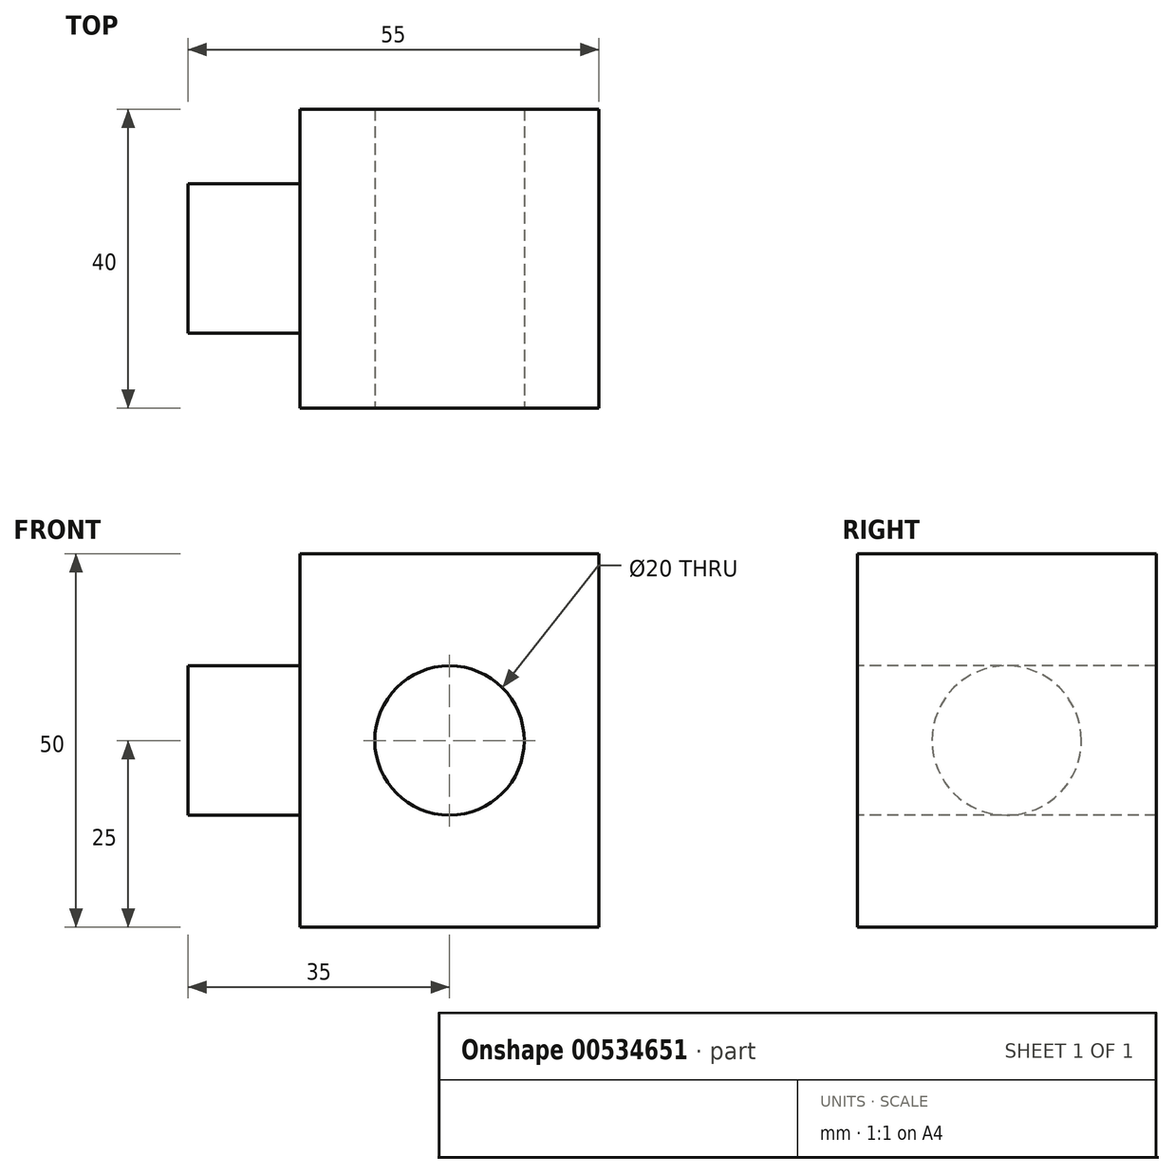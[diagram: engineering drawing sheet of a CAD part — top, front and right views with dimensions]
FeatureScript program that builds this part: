
annotation { "Feature Type Name" : "Feature", "Feature Type Description" : "" }
export const myFeature = defineFeature(function(context is Context, id is Id, definition is map)
    precondition{}
    {
        {
            var Q0;
            Q0=qCreatedBy(makeId("Right.planeOp"),FACE);
            var sketch = newSketch(context, id + "F0", { "sketchPlane" : qUnion([Q0])});
            skLineSegment(sketch, "E0.bottom", {"start": v(-20, 25) * mm, "end": v(20, 25) * mm});
            skLineSegment(sketch, "E0.top", {"start": v(-20, -25) * mm, "end": v(20, -25) * mm});
            skLineSegment(sketch, "E0.left", {"start": v(-20, 25) * mm, "end": v(-20, -25) * mm});
            skLineSegment(sketch, "E0.right", {"start": v(20, 25) * mm, "end": v(20, -25) * mm});
            skCircle(sketch, "E1", {"center": v(0, 0) * mm, "radius": 10 * mm});
            skSolve(sketch);
        }
        {
            var Q0;
            Q0=makeQuery(id+"F0.imprint","IMPRINT",FACE,{"disambiguationData":[TD([[makeQuery(id+"F0.imprint","IMPRINT",EDGE,{"derivedFrom":sQuery(id+"F0.wireOp",EDGE,"E1")}),1.0]])]});
            extrude(context, id + "F1", {"entities" : qUnion([Q0]), "oppositeDirection" : true, "depth" : 15 * mm, "offsetDistance" : 25 * mm});
        }
        {
            var Q0;
            Q0=makeQuery(id+"F0.imprint","IMPRINT",FACE,{"disambiguationData":[TD([[makeQuery(id+"F0.imprint","IMPRINT",EDGE,{"derivedFrom":sQuery(id+"F0.wireOp",EDGE,"E0.bottom")}),-1.0]])]});
            var Q1;
            Q1=makeQuery(id+"F0.imprint","IMPRINT",FACE,{"disambiguationData":[TD([[makeQuery(id+"F0.imprint","IMPRINT",EDGE,{"derivedFrom":sQuery(id+"F0.wireOp",EDGE,"E1")}),1.0]])]});
            extrude(context, id + "F2", {"entities" : qUnion([Q0, Q1]), "operationType" : NewBodyOperationType.ADD, "depth" : 40 * mm, "offsetDistance" : 25 * mm});
        }
        {
            var Q0;
            Q0=makeQuery(id+"F2.opExtrude","SWEPT_FACE",FACE,{"disambiguationData":[OSD([sQuery(id+"F0.wireOp",EDGE,"E0.left")])]});
            var sketch = newSketch(context, id + "F3", { "sketchPlane" : qUnion([Q0])});
            skCircle(sketch, "E2", {"center": v(20, 0) * mm, "radius": 10 * mm});
            skPoint(sketch, "E2.centerSnap0", {"position": v(20, 25) * mm});
            skSolve(sketch);
        }
        {
            var Q0;
            Q0=qSketchRegion(id+"F3",true);
            extrude(context, id + "F4", {"entities" : qUnion([Q0]), "operationType" : NewBodyOperationType.REMOVE, "endBound" : BoundingType.THROUGH_ALL, "oppositeDirection" : true, "depth" : 25 * mm, "offsetDistance" : 25 * mm});
        }
    });
